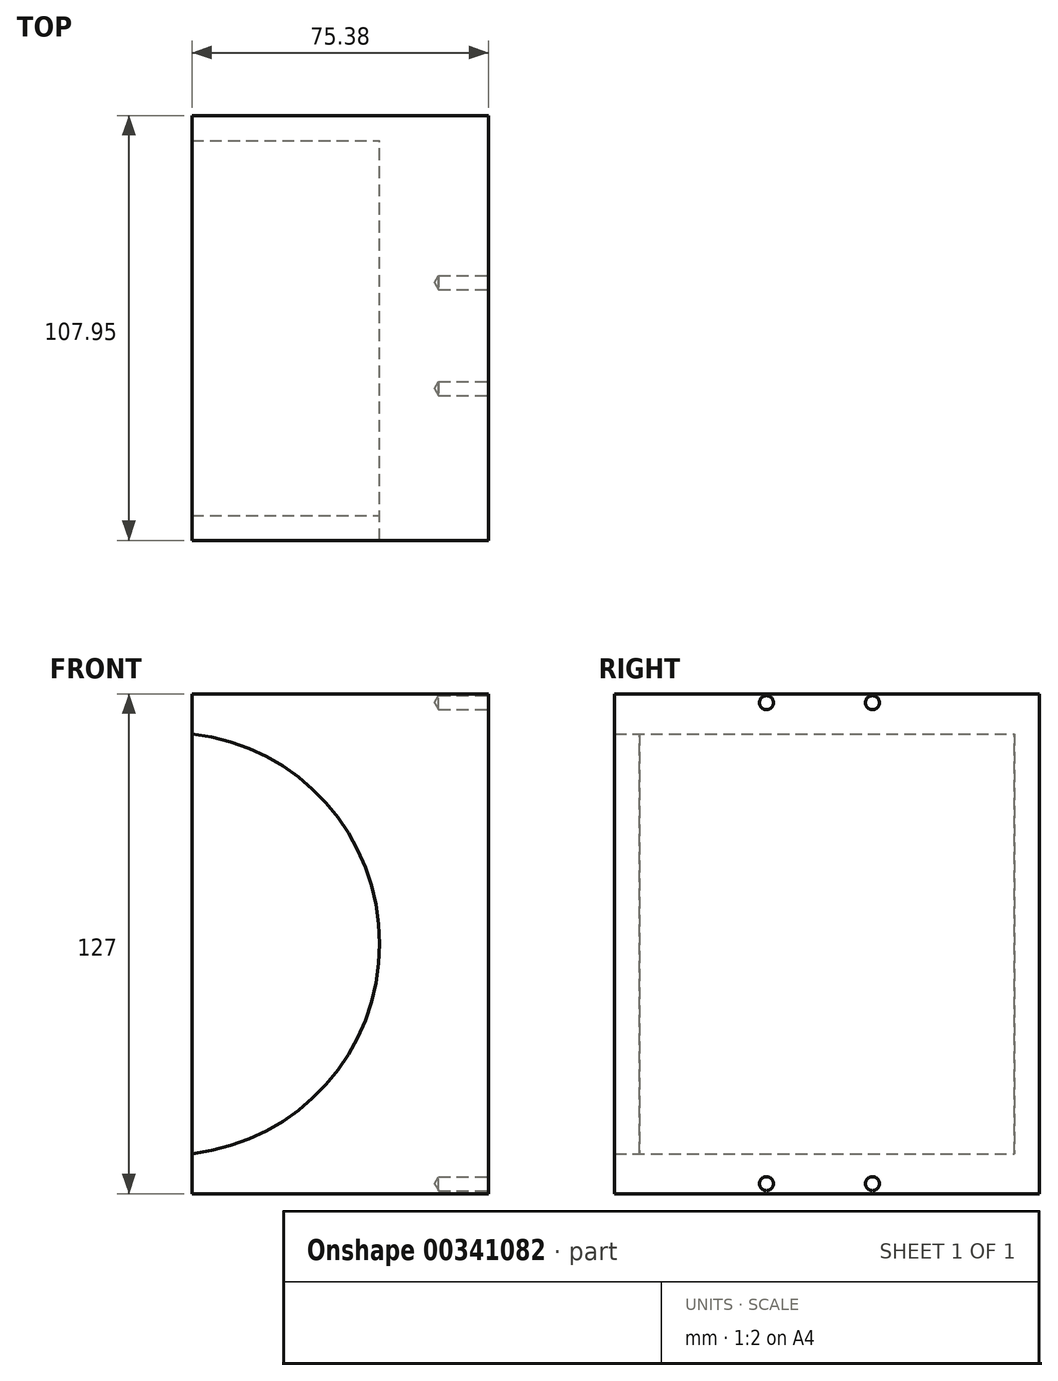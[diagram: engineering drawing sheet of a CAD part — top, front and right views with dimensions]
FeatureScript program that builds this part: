
annotation { "Feature Type Name" : "Feature", "Feature Type Description" : "" }
export const myFeature = defineFeature(function(context is Context, id is Id, definition is map)
    precondition{}
    {
        {
            var Q0;
            Q0=qCreatedBy(makeId("Front.planeOp"),FACE);
            var sketch = newSketch(context, id + "F0", { "sketchPlane" : qUnion([Q0])});
            skCircle(sketch, "E0", {"center": v(-57.66, 0) * mm, "radius": 47.63 * mm});
            skLineSegment(sketch, "E1", {"start": v(0, -53.09) * mm, "end": v(0, -63.25) * mm});
            skLineSegment(sketch, "E2", {"start": v(0, -63.25) * mm, "end": v(75.38, -63.25) * mm});
            skLineSegment(sketch, "E3", {"start": v(0, 53.6) * mm, "end": v(0, 63.75) * mm});
            skLineSegment(sketch, "E4", {"start": v(0, 63.75) * mm, "end": v(75.38, 63.75) * mm});
            skLineSegment(sketch, "E5", {"start": v(75.38, 63.75) * mm, "end": v(75.38, -63.25) * mm});
            skArc(sketch, "E6", {"start": v(0, -53.09) * mm, "mid": v(47.7, 0.25) * mm, "end": v(0, 53.6) * mm});
            skLineSegment(sketch, "E7", {"start": v(0, 53.6) * mm, "end": v(0, -53.09) * mm});
            skSolve(sketch);
        }
        {
            var Q0;
            Q0=makeQuery(id+"F0.imprint","IMPRINT",FACE,{"disambiguationData":[TD([[makeQuery(id+"F0.imprint","IMPRINT",EDGE,{"derivedFrom":sQuery(id+"F0.wireOp",EDGE,"E1")}),1.0]])]});
            extrude(context, id + "F1", {"entities" : qUnion([Q0]), "depth" : 107.95 * mm});
        }
        {
            var Q0;
            Q0=makeQuery(id+"F0.imprint","IMPRINT",FACE,{"disambiguationData":[TD([[makeQuery(id+"F0.imprint","IMPRINT",EDGE,{"derivedFrom":sQuery(id+"F0.wireOp",EDGE,"E6")}),1.0]])]});
            extrude(context, id + "F2", {"entities" : qUnion([Q0]), "operationType" : NewBodyOperationType.ADD, "depth" : 6.35 * mm});
        }
        {
            var Q0;
            Q0=makeQuery(id+"F0.imprint","IMPRINT",FACE,{"disambiguationData":[TD([[makeQuery(id+"F0.imprint","IMPRINT",EDGE,{"derivedFrom":sQuery(id+"F0.wireOp",EDGE,"E6")}),1.0]])]});
            extrude(context, id + "F3", {"entities" : qUnion([Q0]), "depth" : 107.95 * mm, "hasSecondDirection" : true, "secondDirectionOppositeDirection" : false, "secondDirectionDepth" : 101.6 * mm});
        }
        {
            var Q0;
            Q0=makeQuery(id+"F1.opExtrude","SWEPT_FACE",FACE,{"disambiguationData":[OSD([sQuery(id+"F0.wireOp",EDGE,"E5")])]});
            var sketch = newSketch(context, id + "F4", { "sketchPlane" : qUnion([Q0])});
            skCircle(sketch, "E8.5", {"center": v(-42.44, -60.7) * mm, "radius": 1.78 * mm});
            skCircle(sketch, "E8.7", {"center": v(-69.38, -60.7) * mm, "radius": 1.78 * mm});
            skCircle(sketch, "E9.0", {"center": v(-69.38, 61.49) * mm, "radius": 1.78 * mm});
            skCircle(sketch, "E9.2", {"center": v(-42.44, 61.49) * mm, "radius": 1.78 * mm});
            skPoint(sketch, "E10.0", {"position": v(-5.92, -18.15) * mm});
            skSolve(sketch);
        }
        {
            var Q0;
            Q0=sQuery(id+"F4.wireOp",VERTEX,"E9.0.center");
            var Q1;
            Q1=sQuery(id+"F4.wireOp",VERTEX,"E9.2.center");
            var Q2;
            Q2=sQuery(id+"F4.wireOp",VERTEX,"E8.7.center");
            var Q3;
            Q3=sQuery(id+"F4.wireOp",VERTEX,"E8.5.center");
            var Q4;
            Q4=makeQuery(id+"F1.opExtrude","SWEPT_BODY",BODY,{"disambiguationData":[OSD([sQuery(id+"F0.wireOp",EDGE,"E1"),sQuery(id+"F0.wireOp",EDGE,"E2"),sQuery(id+"F0.wireOp",EDGE,"E3"),sQuery(id+"F0.wireOp",EDGE,"E4"),sQuery(id+"F0.wireOp",EDGE,"E5"),sQuery(id+"F0.wireOp",EDGE,"E6")])]});
            hole(context, id + "F5", {"style" : HoleStyle.SIMPLE, "endStyle" : HoleEndStyle.BLIND, "holeDiameter" : 3.56 * mm, "holeDepth" : 12.7 * mm, "isTappedThrough" : true, "tappedDepth" : 12.7 * mm, "tapClearance" : 3, "startFromSketch" : true, "locations" : qUnion([Q0, Q1, Q2, Q3]), "scope" : qUnion([Q4])});
        }
    });
